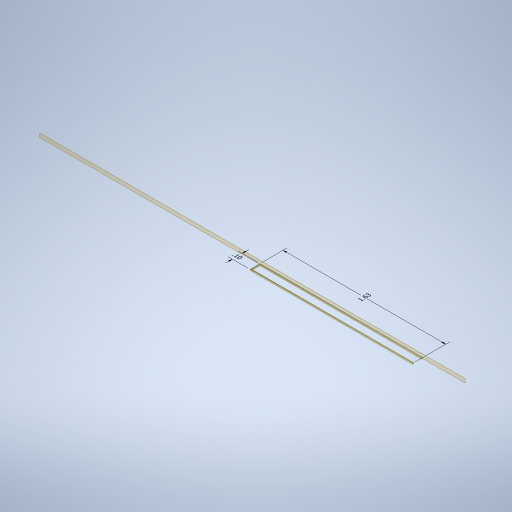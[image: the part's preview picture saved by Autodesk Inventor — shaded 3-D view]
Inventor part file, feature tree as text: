
AUTODESK INVENTOR PART (.ipt)
format: ipt  version: 2024.2 (Build 282272000, 272)  size: 274,944 bytes
history: native  units: in
note: dims shown in document units (in); Inventor stores cm internally (conversion verified against a paired STEP export)
features: other x3, plane x3, sketch x2, sweep x1
ambient origin geometry x8: Origin, YZ Plane, XZ Plane, XY Plane, X Axis, Y Axis, Z Axis, Center Point
bodies: Solid1 (feature_tree)
feature tree (9):
  other  "Annotations"
  sweep  "Sweep1"
  plane  "Work Plane1"
  plane  "Work Plane2"
  plane  "Work Plane4"
  sketch  "Sketch1"  dims[d6=0.0in d7=0.0in d11=0.25in d19=-0.25in]
  sketch  "Sketch2"  dims[d69=1.625in d70=1.625in d86=-0.1175in d89=0.1in d90=0.0in d91=0.0in d92=0.0in d98=0.01in d99=0.01in d100=0.1997in d101=1.625in d102=0.2692in d103=0.1197in d104=0.1in]
  other  "Linear Dimension 1"
  other  "Linear Dimension 2"
